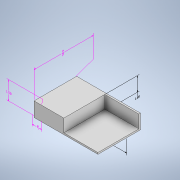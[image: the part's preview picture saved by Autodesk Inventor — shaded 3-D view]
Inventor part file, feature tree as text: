
AUTODESK INVENTOR PART (.ipt)
format: ipt  version: 2021.2 (Build 252289000, 289)  size: 181,248 bytes
history: native  units: in
note: dims shown in document units (in); Inventor stores cm internally (conversion verified against a paired STEP export)
features: other x6, extrude x6, sketch x5
ambient origin geometry x8: Origin, YZ Plane, XZ Plane, XY Plane, X Axis, Y Axis, Z Axis, Center Point
bodies: Solid1 (feature_tree)
feature tree (17):
  other  "Annotations"
  extrude  "Extrusion1"  Depth=3.5in
  extrude  "Extrusion2"  Depth=0.1875in
  extrude  "Extrusion3"  Depth=1.5in
  extrude  "Extrusion4"  TaperAngle=0.0deg  [1 undecoded]
  extrude  "Extrusion5"  Depth=4.0in
  extrude  "Extrusion6"  Depth=4.0in
  sketch  "Sketch2"  dims[d0=5.0in d1=3.5in]
  sketch  "Sketch4"  dims[d2=0.1875in d3=0.0in d4=0.1875in]
  sketch  "Sketch6"  dims[d5=1.5in d6=0.0in d7=0.125in]
  sketch  "Sketch9"  dims[d9=1.5in d10=0.0in]
  sketch  "Sketch10"  dims[d11=0.125in d12=0.125in d13=0.125in d19=1.5in d20=0.0in d37=0.1875in d38=4.0in d39=0.0in d40=4.0in d41=0.0in d49=0.75in d50=0.75in d51=0.5in d31=0.2658in d32=1.6875in d33=0.2063in d34=1.5in d35=0.2057in d36=4.8125in d42=0.117in d43=0.0996in d44=4.0in d47=0.2874in d48=0.75in]
  other  "Linear Dimension 2"
  other  "Linear Dimension 3"
  other  "Linear Dimension 4"
  other  "Linear Dimension 5"
  other  "Linear Dimension 7"
note: 1 required parameter value undecoded (feature->parameter linkage not recoverable at this tier; creation-order binding heuristic only, values carry confidence <= 0.55)
